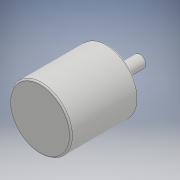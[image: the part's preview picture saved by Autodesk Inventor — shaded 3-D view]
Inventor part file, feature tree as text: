
AUTODESK INVENTOR PART (.ipt)
format: ipt  version: 2017 (Build 210142000, 142)  size: 166,912 bytes
history: native  units: mm
features: sketch x4, extrude x3, other x1, revolve x1, fillet x1
ambient origin geometry x8: Origin, YZ Plane, XZ Plane, XY Plane, X Axis, Y Axis, Z Axis, Center Point
bodies: Body1 (feature_tree)
feature tree (10):
  other  "ソリッド1"
  revolve  "回転1"
  extrude  "押し出し1"  Depth=21.0mm
  extrude  "押し出し2"  Depth=4.0mm
  fillet  "フィレット1"  Radius=12.5mm
  extrude  "押し出し3"  Depth=2.0mm
  sketch  "スケッチ1"
  sketch  "スケッチ2"
  sketch  "スケッチ4"
  sketch  "スケッチ5"
